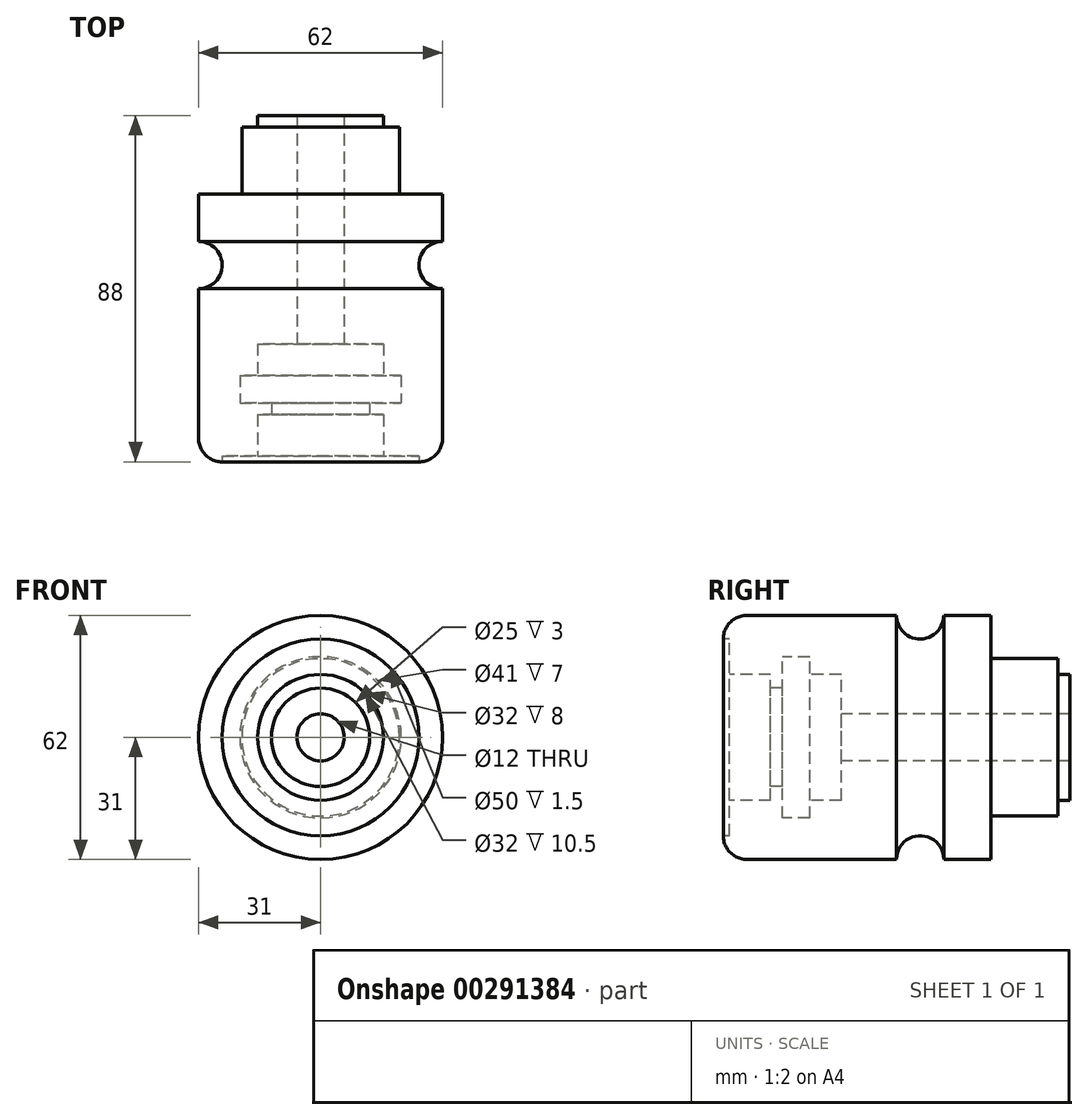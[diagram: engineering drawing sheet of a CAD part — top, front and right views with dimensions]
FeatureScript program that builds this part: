
annotation { "Feature Type Name" : "Feature", "Feature Type Description" : "" }
export const myFeature = defineFeature(function(context is Context, id is Id, definition is map)
    precondition{}
    {
        {
            var Q0;
            Q0=qCreatedBy(makeId("Right.planeOp"),FACE);
            var sketch = newSketch(context, id + "F0", { "sketchPlane" : qUnion([Q0])});
            skLineSegment(sketch, "E0", {"start": v(0, 0) * mm, "end": v(86.3, 0) * mm, "construction": true});
            skLineSegment(sketch, "E1", {"start": v(88, 6) * mm, "end": v(88, 16) * mm});
            skLineSegment(sketch, "E2", {"start": v(85, 16) * mm, "end": v(85, 20) * mm});
            skLineSegment(sketch, "E3", {"start": v(85, 20) * mm, "end": v(68, 20) * mm});
            skLineSegment(sketch, "E4", {"start": v(68, 20) * mm, "end": v(68, 31) * mm});
            skLineSegment(sketch, "E5", {"start": v(68, 31) * mm, "end": v(56, 31) * mm});
            skArc(sketch, "E6", {"start": v(44, 31) * mm, "mid": v(50, 25) * mm, "end": v(56, 31) * mm});
            skLineSegment(sketch, "E7.trimOffspring", {"start": v(44, 31) * mm, "end": v(0, 31) * mm});
            skLineSegment(sketch, "E8", {"start": v(88, 6) * mm, "end": v(30, 6) * mm});
            skLineSegment(sketch, "E9", {"start": v(30, 6) * mm, "end": v(30, 16) * mm});
            skLineSegment(sketch, "E10", {"start": v(30, 16) * mm, "end": v(22, 16) * mm});
            skLineSegment(sketch, "E11", {"start": v(22, 20.5) * mm, "end": v(22, 16) * mm});
            skLineSegment(sketch, "E12", {"start": v(22, 20.5) * mm, "end": v(15, 20.5) * mm});
            skLineSegment(sketch, "E13", {"start": v(15, 12.5) * mm, "end": v(15, 20.5) * mm});
            skLineSegment(sketch, "E14", {"start": v(1.5, 16) * mm, "end": v(1.5, 25) * mm});
            skLineSegment(sketch, "E15", {"start": v(1.5, 25) * mm, "end": v(0, 25) * mm});
            skLineSegment(sketch, "E16", {"start": v(0, 25) * mm, "end": v(0, 31) * mm});
            skLineSegment(sketch, "E17", {"start": v(15, 12.5) * mm, "end": v(12, 12.5) * mm});
            skLineSegment(sketch, "E18", {"start": v(12, 12.5) * mm, "end": v(12, 16) * mm});
            skLineSegment(sketch, "E19", {"start": v(12, 16) * mm, "end": v(1.5, 16) * mm});
            skLineSegment(sketch, "E20", {"start": v(88, 16) * mm, "end": v(85, 16) * mm});
            skSolve(sketch);
        }
        {
            var Q0;
            Q0=makeQuery(id+"F0.imprint","IMPRINT",FACE,{"disambiguationData":[TD([[makeQuery(id+"F0.imprint","IMPRINT",EDGE,{"derivedFrom":sQuery(id+"F0.wireOp",EDGE,"E1")}),1.0]])]});
            var Q1;
            Q1=sQuery(id+"F0.wireOp",EDGE,"E0");
            revolve(context, id + "F1", {"entities" : qUnion([Q0]), "axis" : qUnion([Q1]), "revolveType" : RevolveType.FULL});
        }
        {
            var Q0;
            Q0=makeQuery(id+"F1.opRevolve","SWEPT_EDGE",EDGE,{"disambiguationData":[OSD([sQuery(id+"F0.wireOp",EDGE,"E7.trimOffspring"),sQuery(id+"F0.wireOp",EDGE,"E16")])]});
            fillet(context, id + "F2", {"entities" : qUnion([Q0]), "radius" : 6 * mm, "tangentPropagation" : true, "allowEdgeOverflow" : false});
        }
    });
